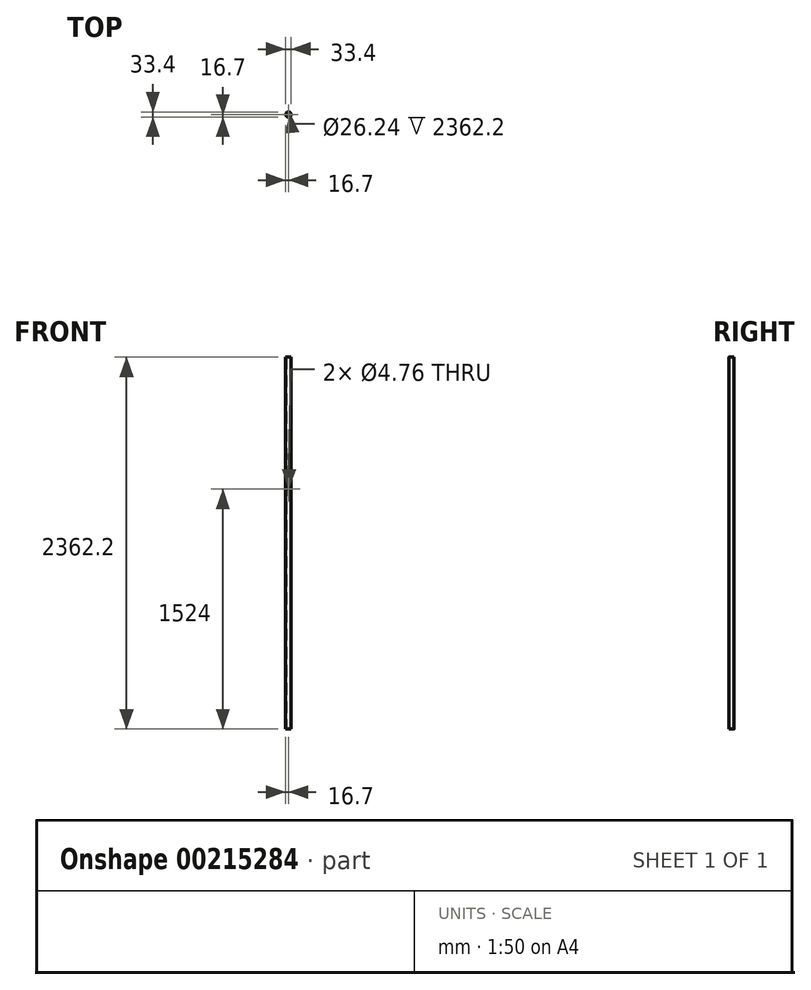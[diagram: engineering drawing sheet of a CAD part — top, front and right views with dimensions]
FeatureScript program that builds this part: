
annotation { "Feature Type Name" : "Feature", "Feature Type Description" : "" }
export const myFeature = defineFeature(function(context is Context, id is Id, definition is map)
    precondition{}
    {
        {
            var Q0;
            Q0=qCreatedBy(makeId("Top.planeOp"),FACE);
            var sketch = newSketch(context, id + "F0", { "sketchPlane" : qUnion([Q0])});
            skCircle(sketch, "E0", {"center": v(0, 0) * mm, "radius": 16.7 * mm});
            skCircle(sketch, "E1", {"center": v(0, 0) * mm, "radius": 13.12 * mm});
            skSolve(sketch);
        }
        {
            var Q0;
            Q0=makeQuery(id+"F0.imprint","IMPRINT",FACE,{"disambiguationData":[TD([[makeQuery(id+"F0.imprint","IMPRINT",EDGE,{"derivedFrom":sQuery(id+"F0.wireOp",EDGE,"E0")}),1.0]])]});
            extrude(context, id + "F1", {"entities" : qUnion([Q0]), "depth" : 2362.2 * mm});
        }
        {
            var Q0;
            Q0=qCreatedBy(makeId("Front.planeOp"),FACE);
            var sketch = newSketch(context, id + "F2", { "sketchPlane" : qUnion([Q0])});
            skCircle(sketch, "E2", {"center": v(0, 1524) * mm, "radius": 2.38 * mm});
            skSolve(sketch);
        }
        {
            var Q0;
            Q0 = qSketchRegion(id + "F2", true);
            extrude(context, id + "F3", {"entities" : qUnion([Q0]), "operationType" : NewBodyOperationType.REMOVE, "endBound" : BoundingType.THROUGH_ALL, "oppositeDirection" : true, "depth" : 25.4 * mm, "hasSecondDirection" : true, "secondDirectionBound" : SecondDirectionBoundingType.THROUGH_ALL, "secondDirectionOppositeDirection" : false, "secondDirectionDepth" : 25.4 * mm});
        }
    });
